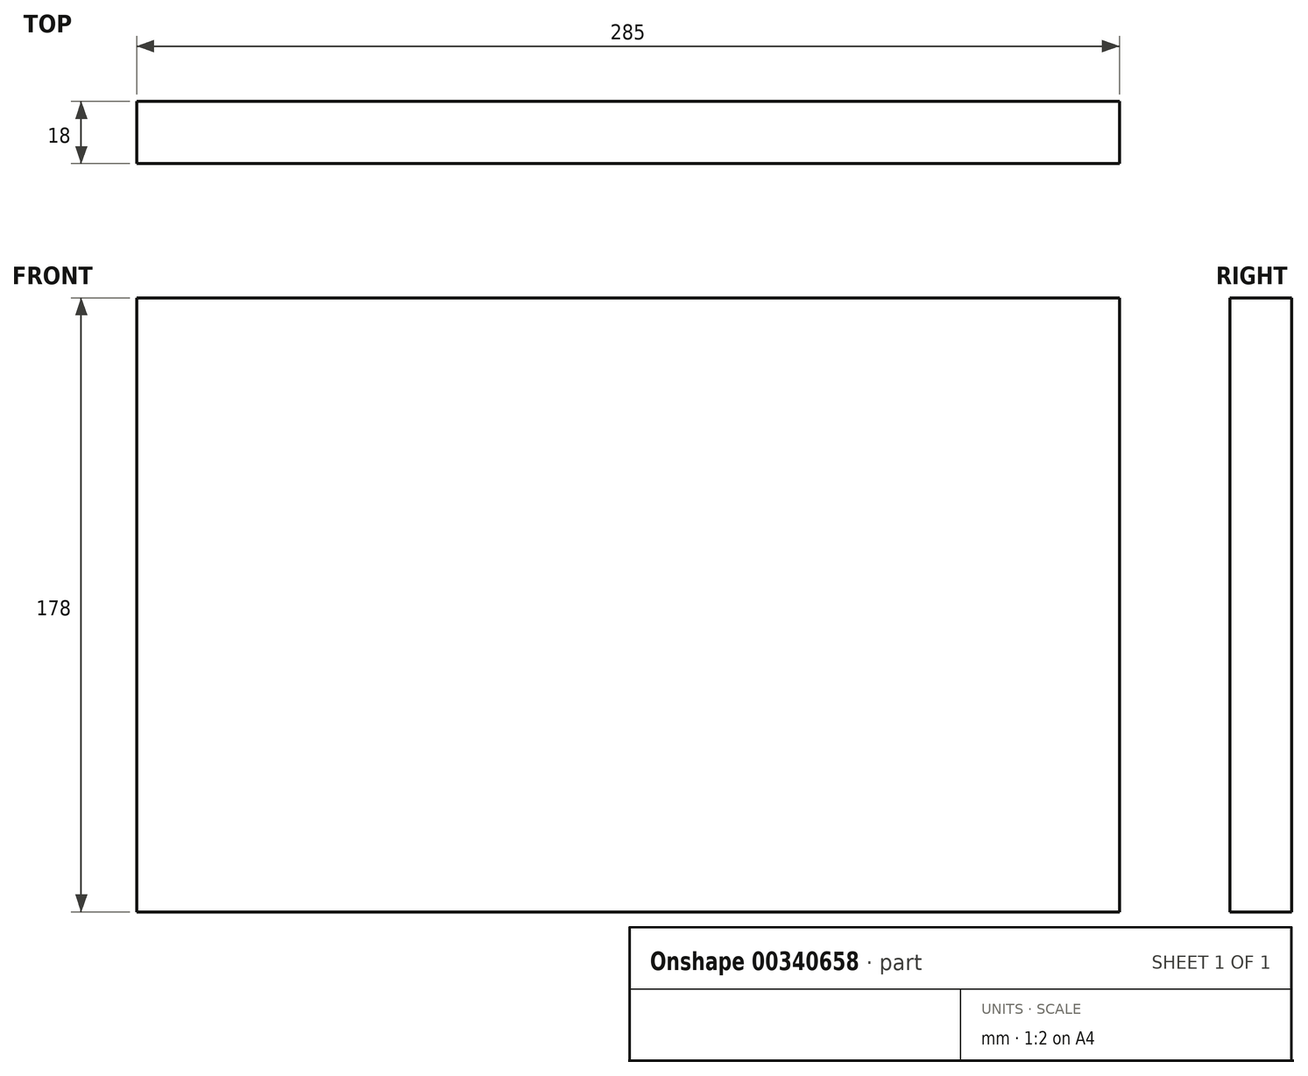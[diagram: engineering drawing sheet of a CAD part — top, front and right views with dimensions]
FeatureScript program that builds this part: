
annotation { "Feature Type Name" : "Feature", "Feature Type Description" : "" }
export const myFeature = defineFeature(function(context is Context, id is Id, definition is map)
    precondition{}
    {
        {
            var Q0;
            Q0=qCreatedBy(makeId("Front.planeOp"),FACE);
            var sketch = newSketch(context, id + "F0", { "sketchPlane" : qUnion([Q0])});
            skLineSegment(sketch, "E0.bottom", {"start": v(-108.76, 122.3) * mm, "end": v(176.24, 122.3) * mm});
            skLineSegment(sketch, "E0.top", {"start": v(-108.76, -55.7) * mm, "end": v(176.24, -55.7) * mm});
            skLineSegment(sketch, "E0.left", {"start": v(-108.76, 122.3) * mm, "end": v(-108.76, -55.7) * mm});
            skLineSegment(sketch, "E0.right", {"start": v(176.24, 122.3) * mm, "end": v(176.24, -55.7) * mm});
            skSolve(sketch);
        }
        {
            var Q0;
            Q0=makeQuery(id+"F0.imprint","IMPRINT",FACE,{"disambiguationData":[TD([[makeQuery(id+"F0.imprint","IMPRINT",EDGE,{"derivedFrom":sQuery(id+"F0.wireOp",EDGE,"E0.bottom")}),-1.0]])]});
            extrude(context, id + "F1", {"entities" : qUnion([Q0]), "depth" : 18 * mm});
        }
    });
